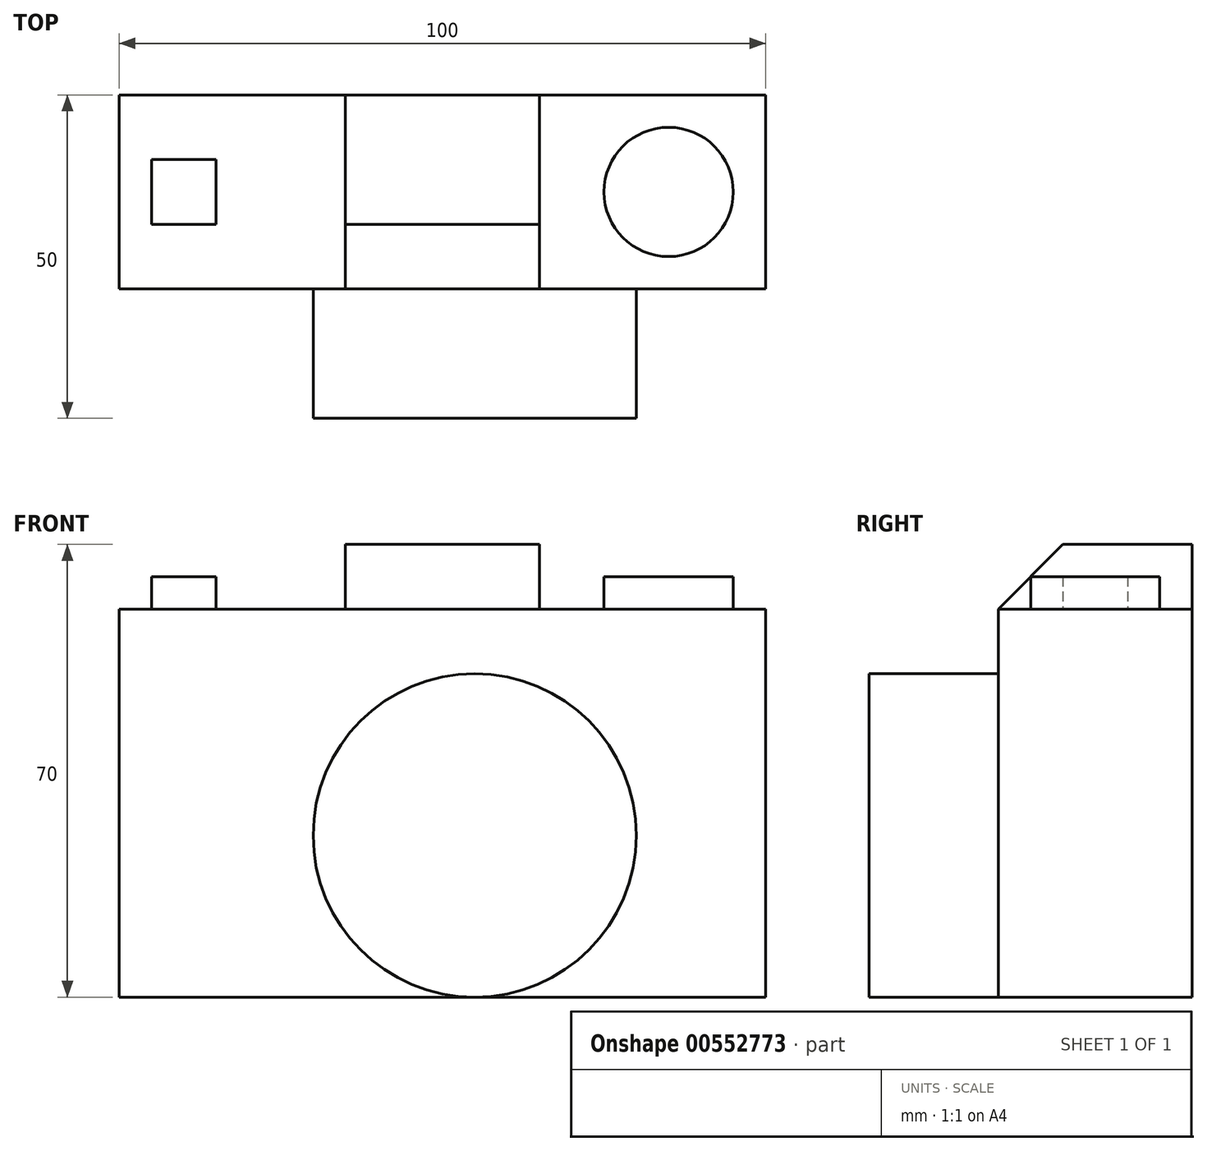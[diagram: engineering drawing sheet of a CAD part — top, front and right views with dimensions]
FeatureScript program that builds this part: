
annotation { "Feature Type Name" : "Feature", "Feature Type Description" : "" }
export const myFeature = defineFeature(function(context is Context, id is Id, definition is map)
    precondition{}
    {
        {
            var Q0;
            Q0=qCreatedBy(makeId("Front.planeOp"),FACE);
            var sketch = newSketch(context, id + "F0", { "sketchPlane" : qUnion([Q0])});
            skCircle(sketch, "E0", {"center": v(0, 0) * mm, "radius": 25 * mm});
            skLineSegment(sketch, "E1.bottom", {"start": v(-55, 35) * mm, "end": v(45, 35) * mm});
            skLineSegment(sketch, "E1.top", {"start": v(-55, -25) * mm, "end": v(45, -25) * mm});
            skLineSegment(sketch, "E1.left", {"start": v(-55, 35) * mm, "end": v(-55, -25) * mm});
            skLineSegment(sketch, "E1.right", {"start": v(45, 35) * mm, "end": v(45, -25) * mm});
            skLineSegment(sketch, "E2.bottom", {"start": v(-20, 35) * mm, "end": v(10, 35) * mm});
            skLineSegment(sketch, "E2.top", {"start": v(-20, 45) * mm, "end": v(10, 45) * mm});
            skLineSegment(sketch, "E2.left", {"start": v(-20, 35) * mm, "end": v(-20, 45) * mm});
            skLineSegment(sketch, "E2.right", {"start": v(10, 35) * mm, "end": v(10, 45) * mm});
            skLineSegment(sketch, "E3", {"start": v(-55, 25) * mm, "end": v(45, 25) * mm});
            skSolve(sketch);
        }
        {
            var Q0;
            Q0 = qSketchRegion(id + "F0", true);
            extrude(context, id + "F1", {"entities" : qUnion([Q0]), "depth" : 30 * mm, "offsetDistance" : 25 * mm});
        }
        {
            var Q0;
            Q0=makeQuery(id+"F1.opExtrude","CAP_FACE",FACE,{"disambiguationData":[OSD([sQuery(id+"F0.wireOp",EDGE,"E1.bottom"),sQuery(id+"F0.wireOp",EDGE,"E1.top"),sQuery(id+"F0.wireOp",EDGE,"E1.left"),sQuery(id+"F0.wireOp",EDGE,"E1.right"),sQuery(id+"F0.wireOp",EDGE,"E2.top"),sQuery(id+"F0.wireOp",EDGE,"E2.left"),sQuery(id+"F0.wireOp",EDGE,"E2.right"),sQuery(id+"F0.wireOp",EDGE,"h7RuicIR-8eDy-ojHR-QEBz-y6BbQtJhnOgG.top"),sQuery(id+"F0.wireOp",EDGE,"h7RuicIR-8eDy-ojHR-QEBz-y6BbQtJhnOgG.left"),sQuery(id+"F0.wireOp",EDGE,"h7RuicIR-8eDy-ojHR-QEBz-y6BbQtJhnOgG.right")])],"isStart":false});
            var sketch = newSketch(context, id + "F2", { "sketchPlane" : qUnion([Q0])});
            skCircle(sketch, "E4", {"center": v(0, 0) * mm, "radius": 25 * mm});
            skSolve(sketch);
        }
        {
            var Q0;
            Q0 = qSketchRegion(id + "F2", true);
            extrude(context, id + "F3", {"entities" : qUnion([Q0]), "operationType" : NewBodyOperationType.ADD, "depth" : 20 * mm, "offsetDistance" : 25 * mm});
        }
        {
            var Q0;
            {var subQ0=sQuery(id+"F0.wireOp",EDGE,"E1.bottom");Q0=makeQuery(id+"F1.opExtrude","SWEPT_FACE",FACE,{"disambiguationData":[OSD([subQ0]),TDD([makeQuery(id+"F0.imprint","IMPRINT",EDGE,{"disambiguationData":[TD([[makeQuery(id+"F0.imprint","INTERSECT",VERTEX,{"derivedFrom":[subQ0,sQuery(id+"F0.wireOp",EDGE,"E1.right")]}),1.0]])],"derivedFrom":subQ0})])]});}
            var sketch = newSketch(context, id + "F4", { "sketchPlane" : qUnion([Q0])});
            skLineSegment(sketch, "E5.bottom", {"start": v(-50, -10) * mm, "end": v(-40, -10) * mm});
            skLineSegment(sketch, "E5.top", {"start": v(-50, -20) * mm, "end": v(-40, -20) * mm});
            skLineSegment(sketch, "E5.left", {"start": v(-50, -10) * mm, "end": v(-50, -20) * mm});
            skLineSegment(sketch, "E5.right", {"start": v(-40, -10) * mm, "end": v(-40, -20) * mm});
            skCircle(sketch, "E6", {"center": v(30, -15) * mm, "radius": 10 * mm});
            skSolve(sketch);
        }
        {
            var Q0;
            Q0 = qSketchRegion(id + "F4", true);
            extrude(context, id + "F5", {"entities" : qUnion([Q0]), "operationType" : NewBodyOperationType.ADD, "depth" : 5 * mm, "offsetDistance" : 25 * mm});
        }
        {
            var Q0;
            Q0=makeQuery(id+"F1.opExtrude","CAP_EDGE",EDGE,{"disambiguationData":[OSD([sQuery(id+"F0.wireOp",EDGE,"E2.top")])],"isStart":false});
            chamfer(context, id + "F6", {"entities" : qUnion([Q0]), "chamferType" : ChamferType.OFFSET_ANGLE, "width" : 10 * mm, "oppositeDirection" : false, "angle" : 45 * degree, "tangentPropagation" : true});
        }
    });
